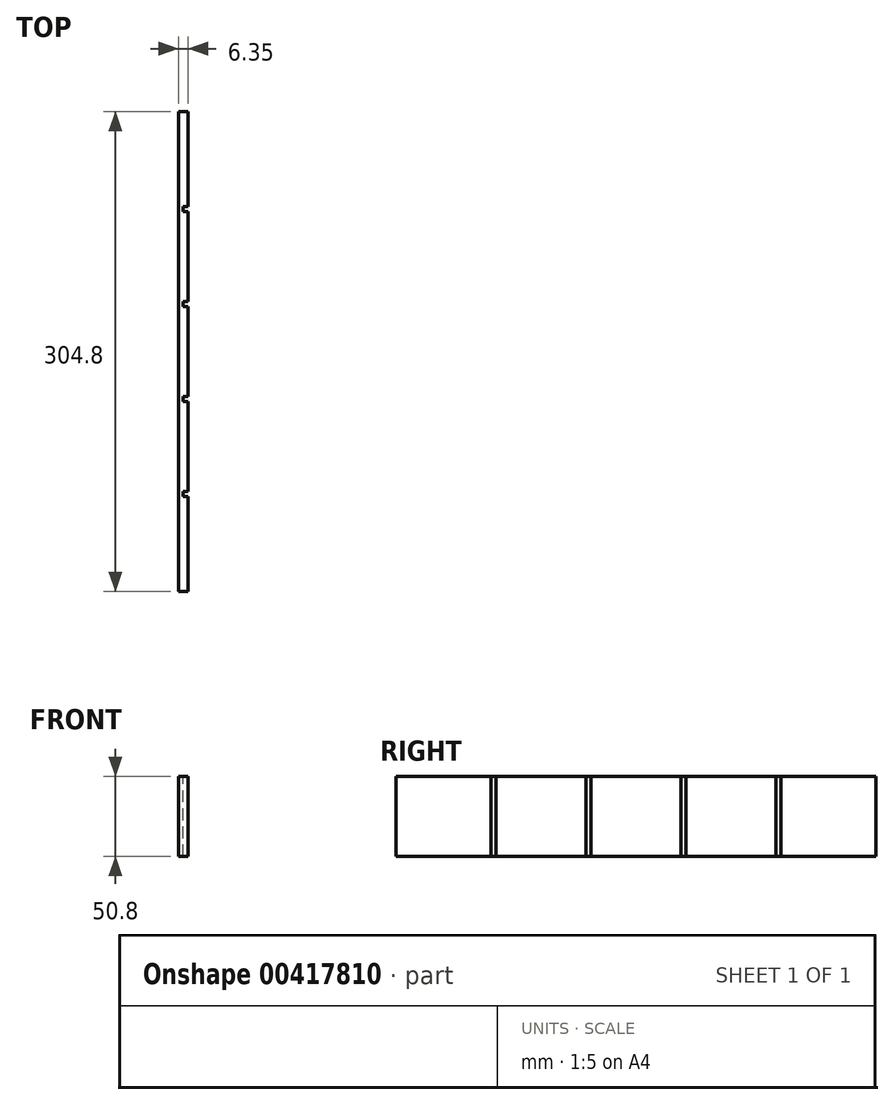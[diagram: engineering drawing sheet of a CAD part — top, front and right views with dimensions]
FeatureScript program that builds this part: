
annotation { "Feature Type Name" : "Feature", "Feature Type Description" : "" }
export const myFeature = defineFeature(function(context is Context, id is Id, definition is map)
    precondition{}
    {
        {
            var Q0;
            Q0=qCreatedBy(makeId("Right.planeOp"),FACE);
            var sketch = newSketch(context, id + "F0", { "sketchPlane" : qUnion([Q0])});
            skLineSegment(sketch, "E0.bottom", {"start": v(-131.06, -53.57) * mm, "end": v(173.74, -53.57) * mm});
            skLineSegment(sketch, "E0.top", {"start": v(-131.06, -2.77) * mm, "end": v(173.74, -2.77) * mm});
            skLineSegment(sketch, "E0.left", {"start": v(-131.06, -53.57) * mm, "end": v(-131.06, -2.77) * mm});
            skLineSegment(sketch, "E0.right", {"start": v(173.74, -53.57) * mm, "end": v(173.74, -2.77) * mm});
            skSolve(sketch);
        }
        {
            var Q0;
            Q0=makeQuery(id+"F0.imprint","IMPRINT",FACE,{"disambiguationData":[TD([[makeQuery(id+"F0.imprint","IMPRINT",EDGE,{"derivedFrom":sQuery(id+"F0.wireOp",EDGE,"E0.bottom")}),1.0]])]});
            extrude(context, id + "F1", {"entities" : qUnion([Q0]), "depth" : 6.35 * mm});
        }
        {
            var Q0;
            Q0=makeQuery(id+"F1.opExtrude","CAP_FACE",FACE,{"disambiguationData":[OSD([sQuery(id+"F0.wireOp",EDGE,"E0.bottom"),sQuery(id+"F0.wireOp",EDGE,"E0.top"),sQuery(id+"F0.wireOp",EDGE,"E0.left"),sQuery(id+"F0.wireOp",EDGE,"E0.right")])],"isStart":false});
            var sketch = newSketch(context, id + "F2", { "sketchPlane" : qUnion([Q0])});
            skLineSegment(sketch, "E1.bottom", {"start": v(-131.06, -53.57) * mm, "end": v(-127.89, -53.57) * mm});
            skLineSegment(sketch, "E1.top", {"start": v(-131.06, -2.77) * mm, "end": v(-127.89, -2.77) * mm});
            skLineSegment(sketch, "E1.left", {"start": v(-131.06, -53.57) * mm, "end": v(-131.06, -2.77) * mm});
            skLineSegment(sketch, "E1.right", {"start": v(-127.89, -53.57) * mm, "end": v(-127.89, -2.77) * mm});
            skLineSegment(sketch, "E2.bottom", {"start": v(-70.74, -53.57) * mm, "end": v(-67.56, -53.57) * mm});
            skLineSegment(sketch, "E2.top", {"start": v(-70.74, -2.77) * mm, "end": v(-67.56, -2.77) * mm});
            skLineSegment(sketch, "E2.left", {"start": v(-70.74, -53.57) * mm, "end": v(-70.74, -2.77) * mm});
            skLineSegment(sketch, "E2.right", {"start": v(-67.56, -53.57) * mm, "end": v(-67.56, -2.77) * mm});
            skLineSegment(sketch, "E3.bottom", {"start": v(-10.41, -53.57) * mm, "end": v(-7.24, -53.57) * mm});
            skLineSegment(sketch, "E3.top", {"start": v(-10.41, -2.77) * mm, "end": v(-7.24, -2.77) * mm});
            skLineSegment(sketch, "E3.left", {"start": v(-10.41, -53.57) * mm, "end": v(-10.41, -2.77) * mm});
            skLineSegment(sketch, "E3.right", {"start": v(-7.24, -53.57) * mm, "end": v(-7.24, -2.77) * mm});
            skLineSegment(sketch, "E4.bottom", {"start": v(49.91, -53.57) * mm, "end": v(53.09, -53.57) * mm});
            skLineSegment(sketch, "E4.top", {"start": v(49.91, -2.77) * mm, "end": v(53.09, -2.77) * mm});
            skLineSegment(sketch, "E4.left", {"start": v(49.91, -53.57) * mm, "end": v(49.91, -2.77) * mm});
            skLineSegment(sketch, "E4.right", {"start": v(53.09, -53.57) * mm, "end": v(53.09, -2.77) * mm});
            skLineSegment(sketch, "E5.bottom", {"start": v(110.24, -53.57) * mm, "end": v(113.41, -53.57) * mm});
            skLineSegment(sketch, "E5.top", {"start": v(110.24, -2.77) * mm, "end": v(113.41, -2.77) * mm});
            skLineSegment(sketch, "E5.left", {"start": v(110.24, -53.57) * mm, "end": v(110.24, -2.77) * mm});
            skLineSegment(sketch, "E5.right", {"start": v(113.41, -53.57) * mm, "end": v(113.41, -2.77) * mm});
            skLineSegment(sketch, "E6.bottom", {"start": v(170.56, -53.57) * mm, "end": v(173.74, -53.57) * mm});
            skLineSegment(sketch, "E6.top", {"start": v(170.56, -2.77) * mm, "end": v(173.74, -2.77) * mm});
            skLineSegment(sketch, "E6.left", {"start": v(170.56, -53.57) * mm, "end": v(170.56, -2.77) * mm});
            skLineSegment(sketch, "E6.right", {"start": v(173.74, -53.57) * mm, "end": v(173.74, -2.77) * mm});
            skSolve(sketch);
        }
        {
            var Q0;
            Q0=makeQuery(id+"F2.imprint","IMPRINT",FACE,{"disambiguationData":[TD([[makeQuery(id+"F2.imprint","IMPRINT",EDGE,{"derivedFrom":sQuery(id+"F2.wireOp",EDGE,"E2.bottom")}),1.0]])]});
            var Q1;
            Q1=makeQuery(id+"F2.imprint","IMPRINT",FACE,{"disambiguationData":[TD([[makeQuery(id+"F2.imprint","IMPRINT",EDGE,{"derivedFrom":sQuery(id+"F2.wireOp",EDGE,"E3.bottom")}),1.0]])]});
            var Q2;
            Q2=makeQuery(id+"F2.imprint","IMPRINT",FACE,{"disambiguationData":[TD([[makeQuery(id+"F2.imprint","IMPRINT",EDGE,{"derivedFrom":sQuery(id+"F2.wireOp",EDGE,"E4.bottom")}),1.0]])]});
            var Q3;
            Q3=makeQuery(id+"F2.imprint","IMPRINT",FACE,{"disambiguationData":[TD([[makeQuery(id+"F2.imprint","IMPRINT",EDGE,{"derivedFrom":sQuery(id+"F2.wireOp",EDGE,"E5.bottom")}),1.0]])]});
            extrude(context, id + "F3", {"entities" : qUnion([Q0, Q1, Q2, Q3]), "operationType" : NewBodyOperationType.REMOVE, "oppositeDirection" : true, "depth" : 3.17 * mm});
        }
    });
